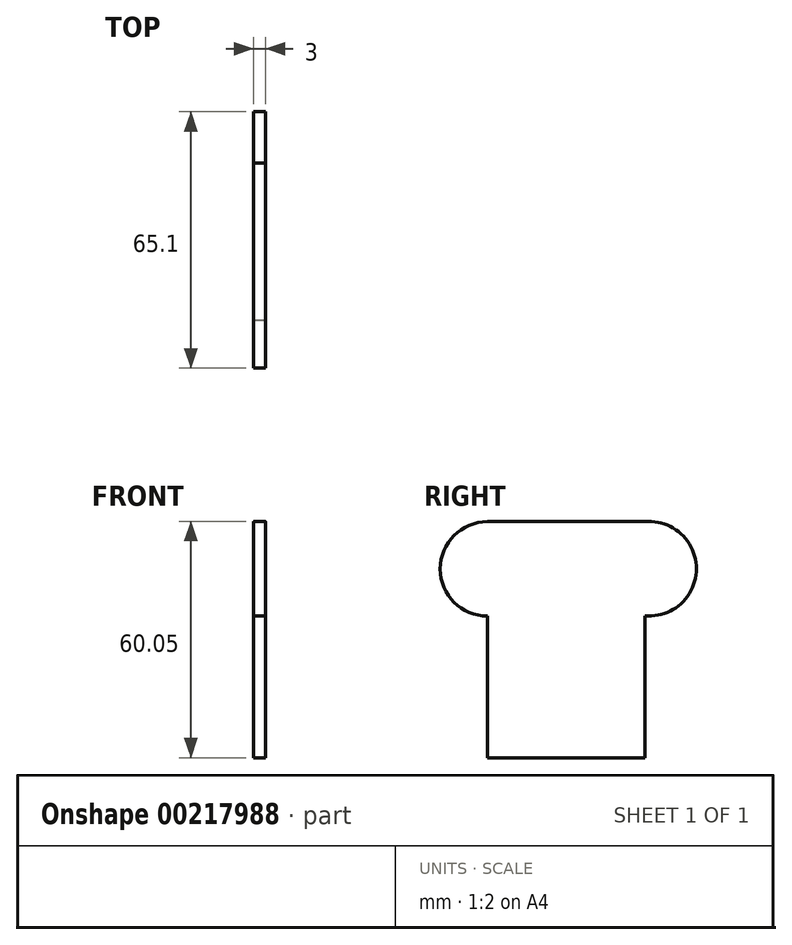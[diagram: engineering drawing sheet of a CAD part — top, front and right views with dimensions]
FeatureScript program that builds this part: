
annotation { "Feature Type Name" : "Feature", "Feature Type Description" : "" }
export const myFeature = defineFeature(function(context is Context, id is Id, definition is map)
    precondition{}
    {
        {
            var Q0;
            Q0=qCreatedBy(makeId("Right.planeOp"),FACE);
            var sketch = newSketch(context, id + "F0", { "sketchPlane" : qUnion([Q0])});
            skLineSegment(sketch, "E0", {"start": v(-25.9, 10.04) * mm, "end": v(-25.9, -25.96) * mm});
            skLineSegment(sketch, "E1", {"start": v(-25.9, -25.96) * mm, "end": v(14.1, -25.96) * mm});
            skLineSegment(sketch, "E2", {"start": v(14.1, -25.96) * mm, "end": v(14.1, 10.14) * mm});
            skArc(sketch, "E3", {"start": v(14.1, 10.14) * mm, "mid": v(27.2, 22.09) * mm, "end": v(14.1, 34.04) * mm});
            skLineSegment(sketch, "E4", {"start": v(-25.9, 34.04) * mm, "end": v(14.1, 34.04) * mm});
            skArc(sketch, "E5", {"start": v(-25.9, 34.04) * mm, "mid": v(-37.9, 22.04) * mm, "end": v(-25.9, 10.04) * mm});
            skSolve(sketch);
        }
        {
            var Q0;
            Q0=qSketchRegion(id+"F0",true);
            extrude(context, id + "F1", {"entities" : qUnion([Q0]), "depth" : 3 * mm});
        }
    });
